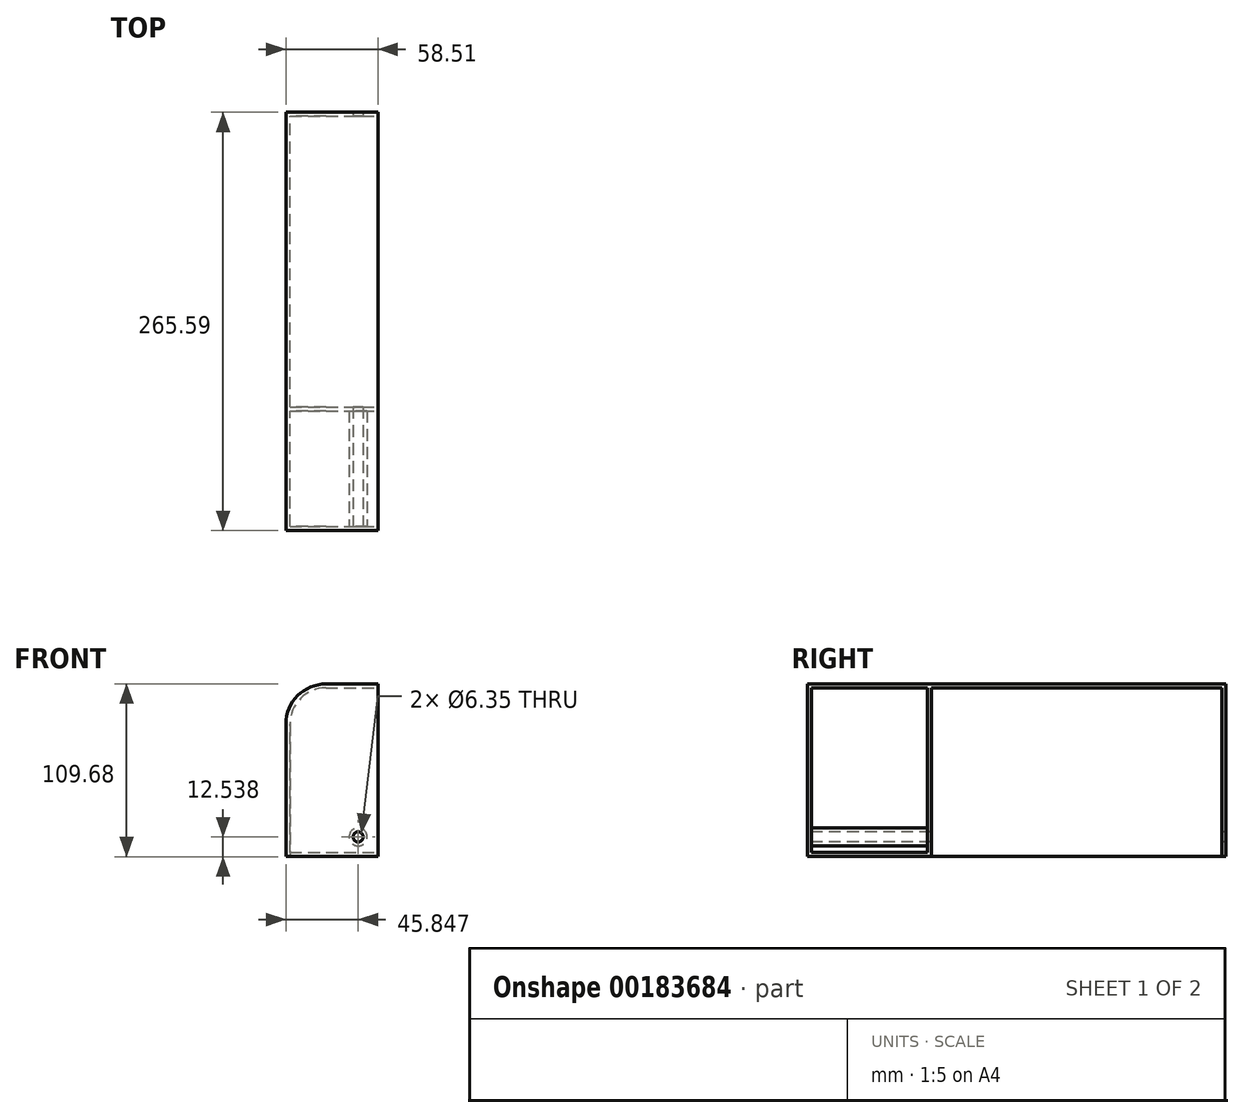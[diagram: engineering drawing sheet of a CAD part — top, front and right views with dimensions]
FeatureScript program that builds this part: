
annotation { "Feature Type Name" : "Feature", "Feature Type Description" : "" }
export const myFeature = defineFeature(function(context is Context, id is Id, definition is map)
    precondition{}
    {
        {
            var Q0;
            Q0=qCreatedBy(makeId("Front.planeOp"),FACE);
            var sketch = newSketch(context, id + "F0", { "sketchPlane" : qUnion([Q0])});
            skLineSegment(sketch, "E0.bottom", {"start": v(-2.65, 60.82) * mm, "end": v(30.46, 60.82) * mm});
            skLineSegment(sketch, "E0.top", {"start": v(-28.05, -48.86) * mm, "end": v(30.46, -48.86) * mm});
            skLineSegment(sketch, "E0.left", {"start": v(-28.05, 35.42) * mm, "end": v(-28.05, -48.86) * mm});
            skLineSegment(sketch, "E0.right", {"start": v(30.46, 60.82) * mm, "end": v(30.46, -48.86) * mm});
            skPoint(sketch, "E1.visualSharp", {"position": v(-28.05, 60.82) * mm});
            skArc(sketch, "E1.filletArc", {"start": v(-2.65, 60.82) * mm, "mid": v(-20.6, 53.38) * mm, "end": v(-28.05, 35.42) * mm});
            skSolve(sketch);
        }
        {
            var Q0;
            Q0=makeQuery(id+"F0.imprint","IMPRINT",FACE,{"disambiguationData":[TD([[makeQuery(id+"F0.imprint","IMPRINT",EDGE,{"derivedFrom":sQuery(id+"F0.wireOp",EDGE,"E0.bottom")}),-1.0]])]});
            extrude(context, id + "F1", {"entities" : qUnion([Q0]), "endBound" : BoundingType.SYMMETRIC, "depth" : 212.5 * mm});
        }
        {
            var Q0;
            Q0=makeQuery(id+"F1.opExtrude","SWEPT_FACE",FACE,{"disambiguationData":[OSD([sQuery(id+"F0.wireOp",EDGE,"E0.right")])]});
            var Q1;
            Q1=makeQuery(id+"F1.opExtrude","SWEPT_FACE",FACE,{"disambiguationData":[OSD([sQuery(id+"F0.wireOp",EDGE,"E0.top")])]});
            shell(context, id + "F2", {"entities" : qUnion([Q0, Q1]), "thickness" : 2.54 * mm});
        }
        {
            var Q0;
            Q0=makeQuery(id+"F1.opExtrude","CAP_FACE",FACE,{"disambiguationData":[OSD([sQuery(id+"F0.wireOp",EDGE,"E0.bottom"),sQuery(id+"F0.wireOp",EDGE,"E0.top"),sQuery(id+"F0.wireOp",EDGE,"E0.left"),sQuery(id+"F0.wireOp",EDGE,"E0.right"),sQuery(id+"F0.wireOp",EDGE,"E1.filletArc")])],"isStart":false});
            var sketch = newSketch(context, id + "F3", { "sketchPlane" : qUnion([Q0])});
            skCircle(sketch, "E2", {"center": v(17.8, -36.32) * mm, "radius": 4.48 * mm});
            skSolve(sketch);
        }
        {
            var Q0;
            Q0=sQuery(id+"F3.wireOp",VERTEX,"E2.center");
            var Q1;
            Q1=makeQuery(id+"F1.opExtrude","SWEPT_BODY",BODY,{"disambiguationData":[OSD([sQuery(id+"F0.wireOp",EDGE,"E0.bottom"),sQuery(id+"F0.wireOp",EDGE,"E0.top"),sQuery(id+"F0.wireOp",EDGE,"E0.left"),sQuery(id+"F0.wireOp",EDGE,"E0.right"),sQuery(id+"F0.wireOp",EDGE,"E1.filletArc")])]});
            hole(context, id + "F4", {"style" : HoleStyle.SIMPLE, "endStyle" : HoleEndStyle.THROUGH, "holeDiameter" : 6.35 * mm, "locations" : qUnion([Q0]), "scope" : qUnion([Q1]), "isTappedThrough" : true});
        }
        {
            var Q0;
            Q0=makeQuery(id+"F1.opExtrude","CAP_FACE",FACE,{"disambiguationData":[OSD([sQuery(id+"F0.wireOp",EDGE,"E0.bottom"),sQuery(id+"F0.wireOp",EDGE,"E0.top"),sQuery(id+"F0.wireOp",EDGE,"E0.left"),sQuery(id+"F0.wireOp",EDGE,"E0.right"),sQuery(id+"F0.wireOp",EDGE,"E1.filletArc")])],"isStart":false});
            var sketch = newSketch(context, id + "F5", { "sketchPlane" : qUnion([Q0])});
            skSolve(sketch);
        }
        {
            var Q0;
            Q0=makeQuery(id+"F5.imprint","IMPRINT",FACE,{"disambiguationData":[TD([[makeQuery(id+"F5.imprint","IMPRINT",EDGE,{"derivedFrom":makeQuery(id+"F1.opExtrude","CAP_EDGE",EDGE,{"disambiguationData":[OSD([sQuery(id+"F0.wireOp",EDGE,"E0.bottom")])],"isStart":false})}),-1.0]])]});
            extrude(context, id + "F6", {"entities" : qUnion([Q0]), "operationType" : NewBodyOperationType.ADD, "depth" : 53.1 * mm, "hasSecondDirection" : true, "secondDirectionOppositeDirection" : true, "secondDirectionDepth" : 25.4 * mm});
        }
        {
            var Q0;
            {var subQ0=sQuery(id+"F0.wireOp",EDGE,"E0.right");Q0=makeQuery(id+"F6.boolean.opBoolean","MERGE",FACE,{"derivedFrom":[makeQuery(id+"F1.opExtrude","SWEPT_FACE",FACE,{"disambiguationData":[OSD([subQ0])]}),makeQuery(id+"F6.opExtrude","SWEPT_FACE",FACE,{"disambiguationData":[OSD([subQ0])]})]});}
            shell(context, id + "F7", {"entities" : qUnion([Q0]), "thickness" : 2.54 * mm});
        }
    });
